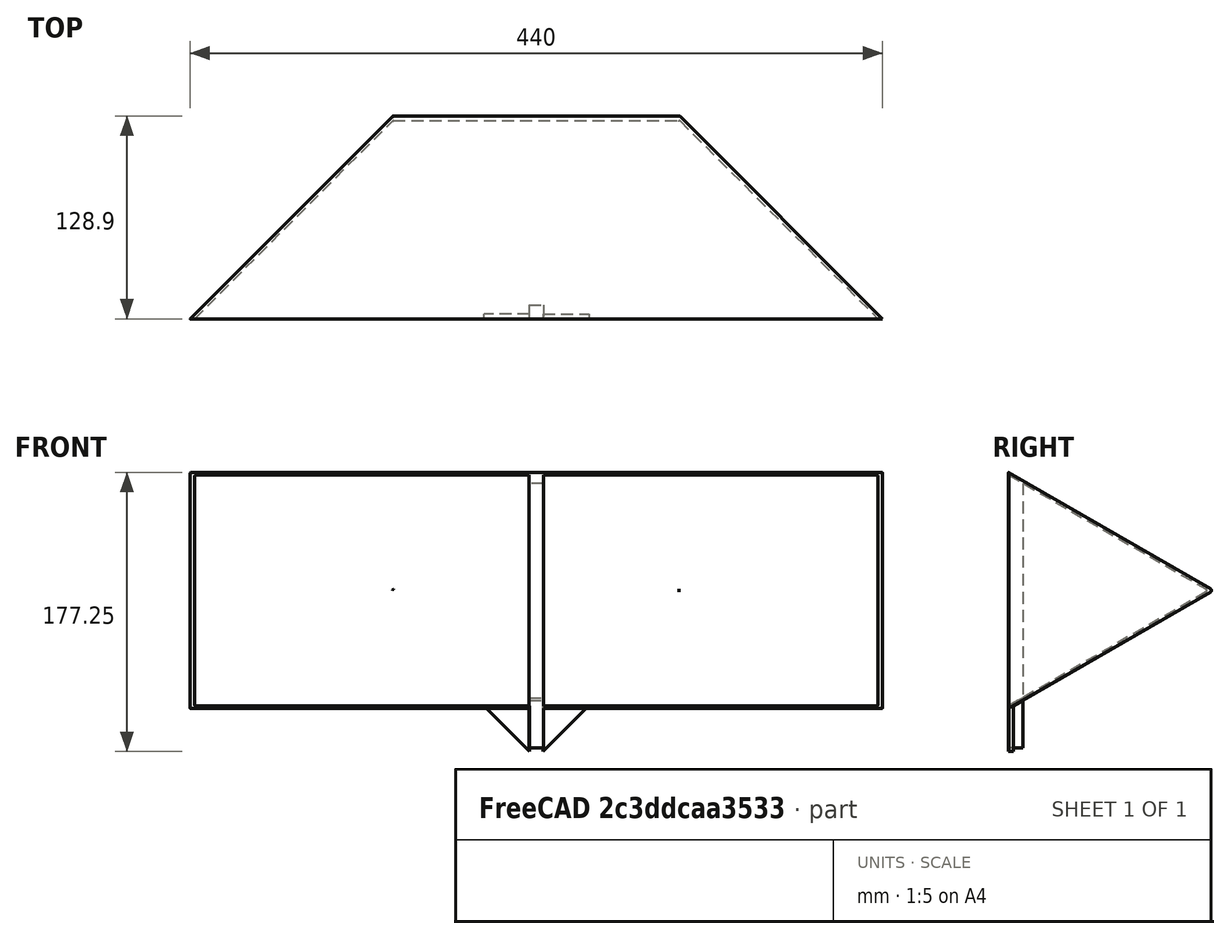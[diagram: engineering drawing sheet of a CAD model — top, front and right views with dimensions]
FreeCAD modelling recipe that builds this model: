
FCSTD DOCUMENT  (FreeCAD 0.18R16110 (Git))
Label: aile
License: All rights reserved
LicenseURL: http://en.wikipedia.org/wiki/All_rights_reserved
objects: Sketcher::SketchObject×6, Part::Extrusion×6, Part::Cut×6, Part::Box×4, Part::Fillet×4, Part::MultiFuse×2, Mesh::Feature×1
note: 28 computed .brp shape members not serialized (recipe doc carries the construction recipe); baked Part::Feature solids carry a one-line shape summary decoded from their .brp

FEATURE [Sketcher::SketchObject] Sketch
  sketch-geometry (3):
    g0: LineSegment StartX=-75 StartY=0 StartZ=0 EndX=0 EndY=129.904 EndZ=0
    g1: LineSegment StartX=0 StartY=129.904 StartZ=0 EndX=75 EndY=0 EndZ=0
    g2: LineSegment StartX=75 StartY=0 StartZ=0 EndX=-75 EndY=0 EndZ=0
  constraints (10):
    c: PointOnObject(g0,g-1)
    c: PointOnObject(g0,g-2)
    c: Coincident(g0,g1)
    c: PointOnObject(g1,g-1)
    c: Coincident(g1,g2)
    c: Coincident(g2,g0)
    c: Equal(g2,g1)
    c: Equal(g0,g1)
    c: Equal(g1,g2)
    c: Distance(g1) = 150
FEATURE [Part::Extrusion] Extrude
  Base = -> Sketch
  Dir = (0,0,1)
  DirMode = 2
  FaceMakerClass = Part::FaceMakerBullseye
  LengthFwd = 440
  LengthRev = 0
  Solid = true
  Symmetric = false
FEATURE [Part::Box] Box  label="Cube"
  AttacherType = Attacher::AttachEngine3D
  Height = 200
  Length = 200
  Placement = pos=(-96,141.421,-141.421) rot=(1,0,0;0.785398rad)
  Width = 200
FEATURE [Part::Cut] Cut
  Base = -> Extrude
  Tool = -> Box
FEATURE [Part::Box] Box001  label="Cube001"
  AttacherType = Attacher::AttachEngine3D
  Height = 200
  Length = 200
  Placement = pos=(-96,139.726,300.357) rot=(1,0,0;0.785398rad)
  Width = 200
FEATURE [Part::Cut] Cut001
  Base = -> Cut
  Tool = -> Box001
FEATURE [Part::Fillet] Fillet
  Base = -> Cut001
  Edges = 5 edges r=1: [Edge1,Edge2,Edge3,Edge6,Edge10]
FEATURE [Part::Fillet] Fillet001
  Base = -> Cut001
  Edges = 5 edges r=1: [Edge1,Edge2,Edge3,Edge6,Edge10]
  Placement = pos=(0,-3,0) rot=(0,0,1;0rad)
FEATURE [Part::Cut] Cut002
  Base = -> Fillet
  Tool = -> Fillet001
FEATURE [Sketcher::SketchObject] Sketch001
  sketch-geometry (4):
    g0: LineSegment StartX=-75 StartY=0 StartZ=0 EndX=-69.8038 EndY=9 EndZ=0
    g1: LineSegment StartX=-69.8038 StartY=9 StartZ=0 EndX=100 EndY=9 EndZ=0
    g2: LineSegment StartX=100 StartY=9 StartZ=0 EndX=100 EndY=0 EndZ=0
    g3: LineSegment StartX=100 StartY=0 StartZ=0 EndX=-75 EndY=0 EndZ=0
  constraints (12):
    c: PointOnObject(g0,g-1)
    c: Coincident(g0,g1)
    c: Horizontal(g1)
    c: Coincident(g1,g2)
    c: PointOnObject(g2,g-1)
    c: Vertical(g2)
    c: Coincident(g2,g3)
    c: Coincident(g3,g0)
    c: Angle(g3,g0) = 1.0472
    c: DistanceX(g0) = -75
    c: DistanceX(g2) = 100
    c: DistanceY(g1) = 9
FEATURE [Part::Extrusion] Extrude001
  Base = -> Sketch001
  Dir = (0,0,1)
  DirMode = 2
  FaceMakerClass = Part::FaceMakerBullseye
  LengthFwd = 9
  LengthRev = 0
  Placement = pos=(0,0,215.5) rot=(0,0,1;0rad)
  Solid = true
  Symmetric = false
FEATURE [Mesh::Feature] hand
  Placement = pos=(114.5,0,163) rot=(1,0,0;0.349066rad)
FEATURE [Part::MultiFuse] Fusion
  Placement = pos=(-105.5,-15.92,333) rot=(0,1,0;1.5708rad)
  Shapes = -> [Cut002,Extrude001]
FEATURE [Sketcher::SketchObject] Sketch002
  MapMode = 3
  Placement = pos=(-105.5,-15.92,333) rot=(0.57735,0.57735,-0.57735;2.0944rad)
  Support = -> [Fusion]
  sketch-geometry (3):
    g0: LineSegment StartX=74.6503 StartY=215.737 StartZ=0 EndX=74.6503 EndY=186.737 EndZ=0
    g1: LineSegment StartX=74.6503 StartY=186.737 StartZ=0 EndX=103.65 EndY=215.737 EndZ=0
    g2: LineSegment StartX=103.65 StartY=215.737 StartZ=0 EndX=74.6503 EndY=215.737 EndZ=0
  constraints (7):
    c: Vertical(g0)
    c: Coincident(g0,g1)
    c: Coincident(g1,g2)
    c: Coincident(g2,g0)
    c: Angle(g0,g2) = 1.5708
    c: Distance(g2) = 29
    c: Distance(g0) = 29
FEATURE [Part::Extrusion] Extrude003
  Base = -> Sketch002
  Dir = (-1e-16,-1,-1e-16)
  DirMode = 2
  FaceMakerClass = Part::FaceMakerBullseye
  LengthFwd = 3
  LengthRev = 0
  Placement = pos=(0,0,1.4) rot=(0,0,1;0rad)
  Reversed = true
  Solid = true
  Symmetric = false
FEATURE [Part::Box] Box002  label="Cube002"
  AttacherType = Attacher::AttachEngine3D
  Height = 200
  Length = 200
  Placement = pos=(-96,139.726,300.357) rot=(1,0,0;0.785398rad)
  Width = 200
FEATURE [Sketcher::SketchObject] Sketch003
  sketch-geometry (4):
    g0: LineSegment StartX=-75 StartY=0 StartZ=0 EndX=-69.8038 EndY=9 EndZ=0
    g1: LineSegment StartX=-69.8038 StartY=9 StartZ=0 EndX=100 EndY=9 EndZ=0
    g2: LineSegment StartX=100 StartY=9 StartZ=0 EndX=100 EndY=0 EndZ=0
    g3: LineSegment StartX=100 StartY=0 StartZ=0 EndX=-75 EndY=0 EndZ=0
  constraints (12):
    c: PointOnObject(g0,g-1)
    c: Coincident(g0,g1)
    c: Horizontal(g1)
    c: Coincident(g1,g2)
    c: PointOnObject(g2,g-1)
    c: Vertical(g2)
    c: Coincident(g2,g3)
    c: Coincident(g3,g0)
    c: Angle(g3,g0) = 1.0472
    c: DistanceX(g0) = -75
    c: DistanceX(g2) = 100
    c: DistanceY(g1) = 9
FEATURE [Sketcher::SketchObject] Sketch004
  sketch-geometry (3):
    g0: LineSegment StartX=-75 StartY=0 StartZ=0 EndX=0 EndY=129.904 EndZ=0
    g1: LineSegment StartX=0 StartY=129.904 StartZ=0 EndX=75 EndY=0 EndZ=0
    g2: LineSegment StartX=75 StartY=0 StartZ=0 EndX=-75 EndY=0 EndZ=0
  constraints (10):
    c: PointOnObject(g0,g-1)
    c: PointOnObject(g0,g-2)
    c: Coincident(g0,g1)
    c: PointOnObject(g1,g-1)
    c: Coincident(g1,g2)
    c: Coincident(g2,g0)
    c: Equal(g2,g1)
    c: Equal(g0,g1)
    c: Equal(g1,g2)
    c: Distance(g1) = 150
FEATURE [Part::Extrusion] Extrude004
  Base = -> Sketch004
  Dir = (0,0,1)
  DirMode = 2
  FaceMakerClass = Part::FaceMakerBullseye
  LengthFwd = 440
  LengthRev = 0
  Solid = true
  Symmetric = false
FEATURE [Part::Box] Box003  label="Cube003"
  AttacherType = Attacher::AttachEngine3D
  Height = 200
  Length = 200
  Placement = pos=(-96,141.421,-141.421) rot=(1,0,0;0.785398rad)
  Width = 200
FEATURE [Part::Cut] Cut003
  Base = -> Extrude004
  Tool = -> Box003
FEATURE [Part::Cut] Cut004
  Base = -> Cut003
  Tool = -> Box002
FEATURE [Part::Fillet] Fillet002
  Base = -> Cut004
  Edges = 5 edges r=1: [Edge1,Edge2,Edge3,Edge6,Edge10]
  Placement = pos=(0,-3,0) rot=(0,0,1;0rad)
FEATURE [Part::Fillet] Fillet003
  Base = -> Cut004
  Edges = 5 edges r=1: [Edge1,Edge2,Edge3,Edge6,Edge10]
FEATURE [Part::Cut] Cut005
  Base = -> Fillet003
  Tool = -> Fillet002
FEATURE [Part::Extrusion] Extrude005
  Base = -> Sketch003
  Dir = (0,0,1)
  DirMode = 2
  FaceMakerClass = Part::FaceMakerBullseye
  LengthFwd = 9
  LengthRev = 0
  Placement = pos=(0,0,215.5) rot=(0,0,1;0rad)
  Solid = true
  Symmetric = false
FEATURE [Part::MultiFuse] Fusion001
  Placement = pos=(-105.5,-15.92,333) rot=(0,1,0;1.5708rad)
  Shapes = -> [Cut005,Extrude005]
FEATURE [Sketcher::SketchObject] Sketch005
  MapMode = 3
  Placement = pos=(-105.5,-15.92,333) rot=(0.57735,0.57735,-0.57735;2.0944rad)
  Support = -> [Fusion001]
  sketch-geometry (3):
    g0: LineSegment StartX=74.6503 StartY=215.737 StartZ=0 EndX=74.6503 EndY=186.737 EndZ=0
    g1: LineSegment StartX=74.6503 StartY=186.737 StartZ=0 EndX=103.65 EndY=215.737 EndZ=0
    g2: LineSegment StartX=103.65 StartY=215.737 StartZ=0 EndX=74.6503 EndY=215.737 EndZ=0
  constraints (7):
    c: Vertical(g0)
    c: Coincident(g0,g1)
    c: Coincident(g1,g2)
    c: Coincident(g2,g0)
    c: Angle(g0,g2) = 1.5708
    c: Distance(g2) = 29
    c: Distance(g0) = 29
FEATURE [Part::Extrusion] Extrude006
  Base = -> Sketch005
  Dir = (-1e-16,-1,-1e-16)
  DirMode = 2
  FaceMakerClass = Part::FaceMakerBullseye
  LengthFwd = 3
  LengthRev = 0
  Placement = pos=(229.1,-28.8,1.4) rot=(0,0,-1;3.14159rad)
  Reversed = true
  Solid = true
  Symmetric = false
